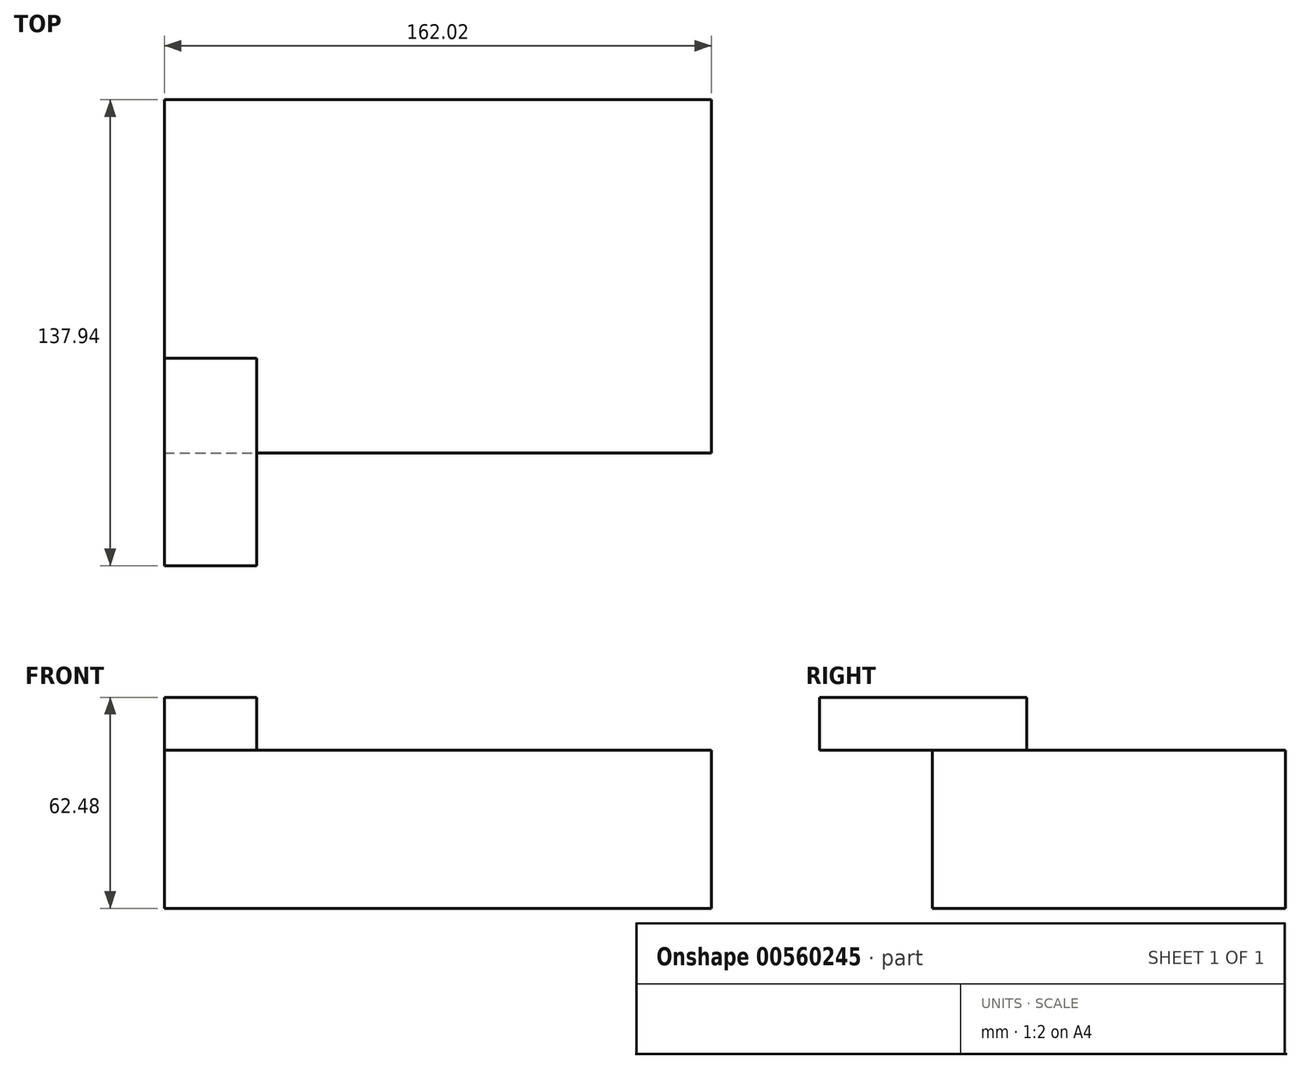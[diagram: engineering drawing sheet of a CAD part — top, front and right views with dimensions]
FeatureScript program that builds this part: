
annotation { "Feature Type Name" : "Feature", "Feature Type Description" : "" }
export const myFeature = defineFeature(function(context is Context, id is Id, definition is map)
    precondition{}
    {
        {
            var Q0;
            Q0=qCreatedBy(makeId("Front.planeOp"),FACE);
            var sketch = newSketch(context, id + "F0", { "sketchPlane" : qUnion([Q0])});
            skLineSegment(sketch, "E0.bottom", {"start": v(52.77, 46.83) * mm, "end": v(0, 46.83) * mm});
            skLineSegment(sketch, "E0.top", {"start": v(52.77, 0) * mm, "end": v(0, 0) * mm});
            skLineSegment(sketch, "E0.left", {"start": v(52.77, 46.83) * mm, "end": v(52.77, 0) * mm});
            skLineSegment(sketch, "E0.right", {"start": v(0, 46.83) * mm, "end": v(0, 0) * mm});
            skSolve(sketch);
        }
        {
            var Q0;
            Q0=makeQuery(id+"F0.imprint","IMPRINT",FACE,{"disambiguationData":[TD([[makeQuery(id+"F0.imprint","IMPRINT",EDGE,{"derivedFrom":sQuery(id+"F0.wireOp",EDGE,"E0.bottom")}),1.0]])]});
            extrude(context, id + "F1", {"entities" : qUnion([Q0]), "depth" : 45.02 * mm, "offsetDistance" : 25.4 * mm});
        }
        {
            var Q0;
            Q0=qCreatedBy(makeId("Right.planeOp"),FACE);
            var sketch = newSketch(context, id + "F2", { "sketchPlane" : qUnion([Q0])});
            skLineSegment(sketch, "E1.bottom", {"start": v(-17.01, 46.8) * mm, "end": v(-78.38, 46.8) * mm});
            skLineSegment(sketch, "E1.top", {"start": v(-17.01, 62.48) * mm, "end": v(-78.38, 62.48) * mm});
            skLineSegment(sketch, "E1.left", {"start": v(-17.01, 46.8) * mm, "end": v(-17.01, 62.48) * mm});
            skLineSegment(sketch, "E1.right", {"start": v(-78.38, 46.8) * mm, "end": v(-78.38, 62.48) * mm});
            skSolve(sketch);
        }
        {
            var Q0;
            Q0 = qSketchRegion(id + "F2", true);
            extrude(context, id + "F3", {"entities" : qUnion([Q0]), "operationType" : NewBodyOperationType.ADD, "depth" : 27.4 * mm, "offsetDistance" : 25.4 * mm});
        }
        {
            var Q0;
            Q0 = qSketchRegion(id + "FjQz50eirqj7Hvc_1", true);
            var Q1;
            Q1=makeQuery(id+"F1.opExtrude","SWEPT_FACE",FACE,{"disambiguationData":[OSD([sQuery(id+"F0.wireOp",EDGE,"E0.left")])]});
            extrude(context, id + "F4", {"entities" : qUnion([Q0, Q1]), "operationType" : NewBodyOperationType.ADD, "depth" : 109.25 * mm, "offsetDistance" : 25.4 * mm});
        }
        {
            var Q0;
            {var subQ0=sQuery(id+"F0.wireOp",EDGE,"E0.left");Q0=makeQuery(id+"F4.boolean.opBoolean","MERGE",FACE,{"derivedFrom":[makeQuery(id+"F1.opExtrude","CAP_FACE",FACE,{"disambiguationData":[OSD([sQuery(id+"F0.wireOp",EDGE,"E0.bottom"),sQuery(id+"F0.wireOp",EDGE,"E0.top"),subQ0,sQuery(id+"F0.wireOp",EDGE,"E0.right")])],"isStart":true}),makeQuery(id+"F4.opExtrude","SWEPT_FACE",FACE,{"disambiguationData":[OSD([subQ0]),TDD([makeQuery(id+"F1.opExtrude","CAP_EDGE",EDGE,{"disambiguationData":[OSD([subQ0])],"isStart":true})])]})]});}
            extrude(context, id + "F5", {"entities" : qUnion([Q0]), "operationType" : NewBodyOperationType.ADD, "depth" : 59.56 * mm, "offsetDistance" : 25.4 * mm});
        }
    });
